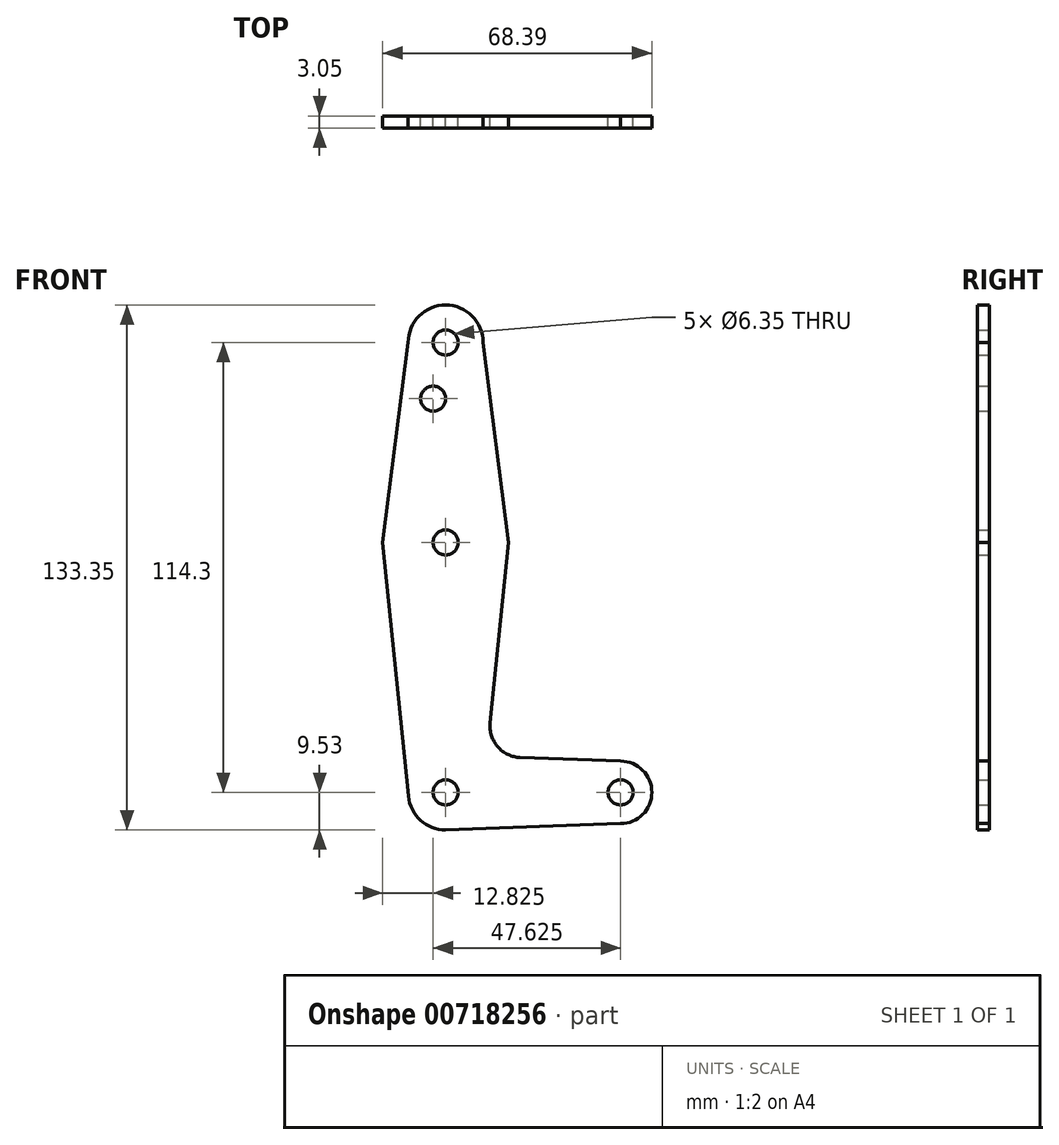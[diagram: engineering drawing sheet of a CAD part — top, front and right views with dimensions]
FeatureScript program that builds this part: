
annotation { "Feature Type Name" : "Feature", "Feature Type Description" : "" }
export const myFeature = defineFeature(function(context is Context, id is Id, definition is map)
    precondition{}
    {
        {
            var Q0;
            Q0=qCreatedBy(makeId("Front.planeOp"),FACE);
            var sketch = newSketch(context, id + "F0", { "sketchPlane" : qUnion([Q0])});
            skCircle(sketch, "E0", {"center": v(0, 0) * mm, "radius": 15.88 * mm});
            skLineSegment(sketch, "E1", {"start": v(0, 0) * mm, "end": v(0, 50.8) * mm});
            skCircle(sketch, "E2", {"center": v(0, 50.8) * mm, "radius": 9.53 * mm});
            skLineSegment(sketch, "E3", {"start": v(0, 0) * mm, "end": v(0, -63.5) * mm});
            skLineSegment(sketch, "E4", {"start": v(0, -63.5) * mm, "end": v(44.45, -63.5) * mm});
            skCircle(sketch, "E5", {"center": v(0, -63.5) * mm, "radius": 9.53 * mm});
            skCircle(sketch, "E6", {"center": v(44.45, -63.5) * mm, "radius": 7.94 * mm});
            skLineSegment(sketch, "E7", {"start": v(-9.53, 50.8) * mm, "end": v(-16, 0) * mm});
            skLineSegment(sketch, "E8", {"start": v(9.53, 50.8) * mm, "end": v(16, 0) * mm});
            skLineSegment(sketch, "E9", {"start": v(16, 0) * mm, "end": v(11.32, -45.9) * mm});
            skLineSegment(sketch, "E10", {"start": v(-16, 0) * mm, "end": v(-9.48, -64.46) * mm});
            skLineSegment(sketch, "E11", {"start": v(18.95, -54.65) * mm, "end": v(44.45, -55.56) * mm});
            skLineSegment(sketch, "E12", {"start": v(44.45, -71.44) * mm, "end": v(0, -73.02) * mm});
            skArc(sketch, "E13.filletArc", {"start": v(11.32, -45.9) * mm, "mid": v(13.24, -51.93) * mm, "end": v(18.95, -54.65) * mm});
            skCircle(sketch, "E14", {"center": v(0, 50.8) * mm, "radius": 3.18 * mm});
            skCircle(sketch, "E15", {"center": v(0, 0) * mm, "radius": 3.18 * mm});
            skCircle(sketch, "E16", {"center": v(0, -63.5) * mm, "radius": 3.18 * mm});
            skCircle(sketch, "E17", {"center": v(44.45, -63.5) * mm, "radius": 3.18 * mm});
            skCircle(sketch, "E18", {"center": v(-3.18, 36.53) * mm, "radius": 3.18 * mm});
            skSolve(sketch);
        }
        {
            var Q0;
            Q0=makeQuery(id+"F0.imprint","IMPRINT",FACE,{"disambiguationData":[TD([[makeQuery(id+"F0.imprint","IMPRINT",EDGE,{"derivedFrom":sQuery(id+"F0.wireOp",EDGE,"E14")}),-1.0]])]});
            var Q1;
            {var subQ5=sQuery(id+"F0.wireOp",EDGE,"E18");Q1=makeQuery(id+"F0.imprint","IMPRINT",FACE,{"disambiguationData":[TD([[makeQuery(id+"F0.imprint","IMPRINT",EDGE,{"derivedFrom":subQ5}),-1.0]])]});}
            var Q2;
            {var subQ4=sQuery(id+"F0.wireOp",EDGE,"E8");var subQ6=sQuery(id+"F0.wireOp",EDGE,"E0");var subQ7=makeQuery(id+"F0.imprint","INTERSECT",VERTEX,{"derivedFrom":[subQ6,subQ4]});Q2=makeQuery(id+"F0.imprint","IMPRINT",FACE,{"disambiguationData":[TD([[makeQuery(id+"F0.imprint","IMPRINT",EDGE,{"disambiguationData":[TD([[subQ7,-1.0]])],"derivedFrom":subQ6}),-1.0]])]});}
            var Q3;
            {var subQ1=sQuery(id+"F0.wireOp",EDGE,"E0");var subQ5=makeQuery(id+"F0.imprint","INTERSECT",VERTEX,{"derivedFrom":[subQ1,sQuery(id+"F0.wireOp",EDGE,"E8")]});Q3=makeQuery(id+"F0.imprint","IMPRINT",FACE,{"disambiguationData":[TD([[makeQuery(id+"F0.imprint","IMPRINT",EDGE,{"disambiguationData":[TD([[subQ5,-1.0]])],"derivedFrom":subQ1}),1.0]])]});}
            var Q4;
            {var subQ1=sQuery(id+"F0.wireOp",EDGE,"E0");var subQ8=makeQuery(id+"F0.imprint","INTERSECT",VERTEX,{"derivedFrom":[subQ1,sQuery(id+"F0.wireOp",EDGE,"E7")]});Q4=makeQuery(id+"F0.imprint","IMPRINT",FACE,{"disambiguationData":[TD([[makeQuery(id+"F0.imprint","IMPRINT",EDGE,{"disambiguationData":[TD([[subQ8,1.0]])],"derivedFrom":subQ1}),1.0]])]});}
            var Q5;
            {var subQ0=sQuery(id+"F0.wireOp",EDGE,"E10");Q5=makeQuery(id+"F0.imprint","IMPRINT",FACE,{"disambiguationData":[TD([[makeQuery(id+"F0.imprint","IMPRINT",EDGE,{"derivedFrom":subQ0}),1.0]])]});}
            var Q6;
            {var subQ5=sQuery(id+"F0.wireOp",EDGE,"E9");Q6=makeQuery(id+"F0.imprint","IMPRINT",FACE,{"disambiguationData":[TD([[makeQuery(id+"F0.imprint","IMPRINT",EDGE,{"derivedFrom":subQ5}),-1.0]])]});}
            var Q7;
            {var subQ0=sQuery(id+"F0.wireOp",EDGE,"E5");var subQ1=sQuery(id+"F0.wireOp",EDGE,"E3");var subQ2=makeQuery(id+"F0.imprint","INTERSECT",VERTEX,{"derivedFrom":[subQ1,subQ0]});Q7=makeQuery(id+"F0.imprint","IMPRINT",FACE,{"disambiguationData":[TD([[makeQuery(id+"F0.imprint","IMPRINT",EDGE,{"disambiguationData":[TD([[subQ2,-1.0]])],"derivedFrom":subQ1}),1.0]])]});}
            var Q8;
            {var subQ0=sQuery(id+"F0.wireOp",EDGE,"E5");var subQ4=sQuery(id+"F0.wireOp",EDGE,"E3");var subQ5=makeQuery(id+"F0.imprint","INTERSECT",VERTEX,{"derivedFrom":[subQ4,subQ0]});Q8=makeQuery(id+"F0.imprint","IMPRINT",FACE,{"disambiguationData":[TD([[makeQuery(id+"F0.imprint","IMPRINT",EDGE,{"disambiguationData":[TD([[subQ5,-1.0]])],"derivedFrom":subQ4}),-1.0]])]});}
            var Q9;
            {var subQ0=sQuery(id+"F0.wireOp",EDGE,"E6");var subQ1=sQuery(id+"F0.wireOp",EDGE,"E4");var subQ2=makeQuery(id+"F0.imprint","INTERSECT",VERTEX,{"derivedFrom":[subQ1,subQ0]});Q9=makeQuery(id+"F0.imprint","IMPRINT",FACE,{"disambiguationData":[TD([[makeQuery(id+"F0.imprint","IMPRINT",EDGE,{"disambiguationData":[TD([[subQ2,1.0]])],"derivedFrom":subQ1}),-1.0]])]});}
            var Q10;
            Q10=makeQuery(id+"F0.imprint","IMPRINT",FACE,{"disambiguationData":[TD([[makeQuery(id+"F0.imprint","IMPRINT",EDGE,{"derivedFrom":sQuery(id+"F0.wireOp",EDGE,"E17")}),-1.0]])]});
            extrude(context, id + "F1", {"entities" : qUnion([Q0, Q1, Q2, Q3, Q4, Q5, Q6, Q7, Q8, Q9, Q10]), "depth" : 3.05 * mm, "offsetDistance" : 25.4 * mm});
        }
    });
